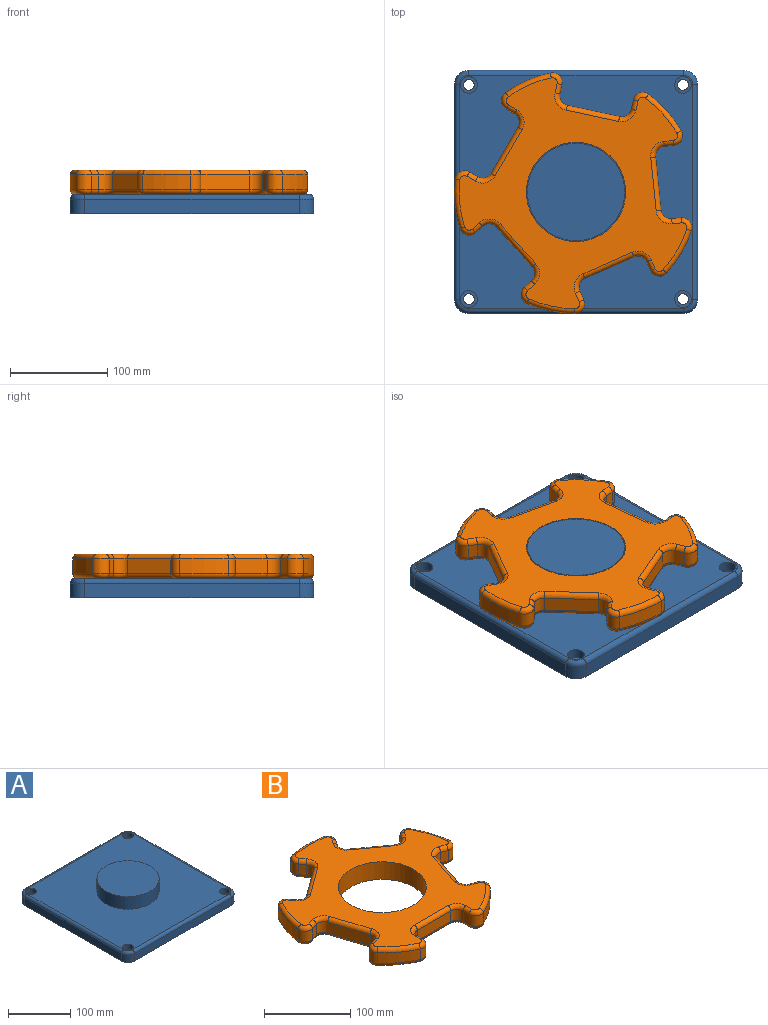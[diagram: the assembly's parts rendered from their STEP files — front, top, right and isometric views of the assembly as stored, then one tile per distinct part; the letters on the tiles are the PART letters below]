
ASSEMBLY  parts=2 mates=1
PART A: 32 faces, bbox 252.5x252.5x45 mm
  f0: plane 220x15mm, normal (1,0,0), area 3300mm2, adj f5,f8,f11,f27
  f1: plane 220x15mm, normal (0,1,0), area 3300mm2, adj f5,f8,f9,f31
  f2: plane 220x15mm, normal (-1,0,0), area 3300mm2, adj f5,f9,f10,f28
  f3: plane 220x15mm, normal (0,-1,0), area 3300mm2, adj f5,f10,f11,f24
  f4: plane 240x240mm, normal (0,0,1), area 48725.4mm2, adj f6,f14,f17,f20,f23,f24,f25,f26
  f5: plane 250x250mm, normal (0,0,-1), area 61926.7mm2, adj f0,f1,f2,f3,f8,f9,f10,f11
  f6: cylinder r=50mm len=100mm, axis (0,0,-1), area 7854mm2, adj f4,f7
  f7: plane 100x100mm, normal (0,0,1), area 7854mm2, adj f6
  f8: cylinder r=15mm len=15mm, axis (0,0,-1), area 353.4mm2, adj f0,f1,f5,f29
  f9: cylinder r=15mm len=15mm, axis (0,0,1), area 353.4mm2, adj f1,f2,f5,f30
  f10: cylinder r=15mm len=15mm, axis (0,0,-1), area 353.4mm2, adj f2,f3,f5,f26
  f11: cylinder r=15mm len=15mm, axis (0,0,1), area 353.4mm2, adj f0,f3,f5,f25
  f12: cylinder r=5.5mm len=11mm, axis (0,0,1), area 345.6mm2, adj f5,f13
  f13: plane 17.25x17.25mm, normal (0,0,1), area 138.7mm2, adj f12,f14
  f14: cylinder r=8.62mm len=17.25mm, axis (0,0,1), area 541.9mm2, adj f4,f13
  f15: cylinder r=5.5mm len=11mm, axis (0,0,1), area 345.6mm2, adj f5,f16
  f16: plane 17.25x17.25mm, normal (0,0,1), area 138.7mm2, adj f15,f17
  f17: cylinder r=8.62mm len=17.25mm, axis (0,0,1), area 541.9mm2, adj f4,f16
  f18: cylinder r=5.5mm len=11mm, axis (0,0,1), area 345.6mm2, adj f5,f19
  f19: plane 17.25x17.25mm, normal (0,0,1), area 138.7mm2, adj f18,f20
  f20: cylinder r=8.62mm len=17.25mm, axis (0,0,1), area 541.9mm2, adj f4,f19
  f21: cylinder r=5.5mm len=11mm, axis (0,0,1), area 345.6mm2, adj f5,f22
  f22: plane 17.25x17.25mm, normal (0,0,1), area 138.7mm2, adj f21,f23
  f23: cylinder r=8.62mm len=17.25mm, axis (0,0,1), area 541.9mm2, adj f4,f22
  f24: cylinder r=5mm len=220mm, axis (-1,0,0), area 1727.9mm2, adj f3,f4,f25,f26
  f25: torus R=10mm, axis (0,0,1), area 162.6mm2, adj f4,f11,f24,f27
  f26: torus R=10mm, axis (0,0,1), area 162.6mm2, adj f4,f10,f24,f28
  f27: cylinder r=5mm len=220mm, axis (0,-1,0), area 1727.9mm2, adj f0,f4,f25,f29
  f28: cylinder r=5mm len=220mm, axis (0,1,0), area 1727.9mm2, adj f2,f4,f26,f30
  f29: torus R=10mm, axis (0,0,1), area 162.6mm2, adj f4,f8,f27,f31
  f30: torus R=10mm, axis (0,0,1), area 162.6mm2, adj f4,f9,f28,f31
  f31: cylinder r=5mm len=220mm, axis (1,0,0), area 1727.9mm2, adj f1,f4,f29,f30
PART B: 123 faces, bbox 268.9x258.5x25 mm
  f0: plane 238.57x229.73mm, normal (0,0,1), area 21505.7mm2, adj f6,f43,f44,f45,f46,f47,f48,f49
  f1: plane 238.57x229.73mm, normal (0,0,-1), area 21505.7mm2, adj f6,f83,f84,f85,f86,f87,f88,f89
  f2: cylinder r=125mm len=40.68mm, axis (0,0,-1), area 759.5mm2, adj f13,f42,f51,f91
  f3: cylinder r=125mm len=47.82mm, axis (0,0,-1), area 759.5mm2, adj f35,f41,f67,f107
  f4: cylinder r=125mm len=50.29mm, axis (0,0,-1), area 759.5mm2, adj f28,f34,f82,f122
  f5: cylinder r=125mm len=47.82mm, axis (0,0,-1), area 759.5mm2, adj f21,f27,f66,f106
  f6: cylinder r=51mm len=102mm, axis (0,0,-1), area 8011.1mm2, adj f0,f1
  f7: cylinder r=125mm len=40.68mm, axis (0,0,-1), area 759.5mm2, adj f14,f20,f50,f90
  f8: plane 15x9.73mm, normal (-1,0,0), area 146mm2, adj f11,f14,f46,f86
  f9: plane 55x15mm, normal (0,-1,0), area 825mm2, adj f11,f12,f43,f83
  f10: plane 15x9.73mm, normal (1,0,0), area 146mm2, adj f12,f13,f47,f87
  f11: cylinder r=10mm len=15mm, axis (0,0,-1), area 235.6mm2, adj f8,f9,f44,f84
  f12: cylinder r=10mm len=15mm, axis (0,0,-1), area 235.6mm2, adj f9,f10,f45,f85
  f13: cylinder r=10mm len=15mm, axis (0,0,-1), area 299.5mm2, adj f2,f10,f49,f89
  f14: cylinder r=10mm len=15mm, axis (0,0,-1), area 299.5mm2, adj f7,f8,f48,f88
  f15: plane 15x9.26mm, normal (-0.31,-0.95,0), area 146mm2, adj f18,f21,f62,f102
  f16: plane 52.31x17mm, normal (0.95,-0.31,0), area 825mm2, adj f18,f19,f58,f98
  f17: plane 15x9.26mm, normal (0.31,0.95,0), area 146mm2, adj f19,f20,f54,f94
  f18: cylinder r=10mm len=15mm, axis (0,0,-1), area 235.6mm2, adj f15,f16,f60,f100
  f19: cylinder r=10mm len=15mm, axis (0,0,-1), area 235.6mm2, adj f16,f17,f56,f96
  f20: cylinder r=10mm len=16.25mm, axis (0,0,-1), area 299.5mm2, adj f7,f17,f52,f92
  f21: cylinder r=10mm len=15mm, axis (0,0,-1), area 299.5mm2, adj f5,f15,f64,f104
  f22: plane 15x7.87mm, normal (0.81,-0.59,0), area 146mm2, adj f25,f28,f78,f118
  f23: plane 44.5x32.33mm, normal (0.59,0.81,0), area 825mm2, adj f25,f26,f74,f114
  f24: plane 15x7.87mm, normal (-0.81,0.59,0), area 146mm2, adj f26,f27,f70,f110
  f25: cylinder r=10mm len=15mm, axis (0,0,-1), area 235.6mm2, adj f22,f23,f76,f116
  f26: cylinder r=10mm len=15mm, axis (0,0,-1), area 235.6mm2, adj f23,f24,f72,f112
  f27: cylinder r=10mm len=16.78mm, axis (0,0,-1), area 299.5mm2, adj f5,f24,f68,f108
  f28: cylinder r=10mm len=15.67mm, axis (0,0,-1), area 299.5mm2, adj f4,f22,f80,f120
  f29: plane 15x7.87mm, normal (0.81,0.59,0), area 146mm2, adj f32,f35,f71,f111
  f30: plane 44.5x32.33mm, normal (-0.59,0.81,0), area 825mm2, adj f32,f33,f75,f115
  f31: plane 15x7.87mm, normal (-0.81,-0.59,0), area 146mm2, adj f33,f34,f79,f119
  f32: cylinder r=10mm len=15mm, axis (0,0,-1), area 235.6mm2, adj f29,f30,f73,f113
  f33: cylinder r=10mm len=15mm, axis (0,0,-1), area 235.6mm2, adj f30,f31,f77,f117
  f34: cylinder r=10mm len=15.67mm, axis (0,0,-1), area 299.5mm2, adj f4,f31,f81,f121
  f35: cylinder r=10mm len=16.78mm, axis (0,0,-1), area 299.5mm2, adj f3,f29,f69,f109
  f36: plane 15x9.26mm, normal (-0.31,0.95,0), area 146mm2, adj f39,f42,f55,f95
  f37: plane 52.31x17mm, normal (-0.95,-0.31,0), area 825mm2, adj f39,f40,f59,f99
  f38: plane 15x9.26mm, normal (0.31,-0.95,0), area 146mm2, adj f40,f41,f63,f103
  f39: cylinder r=10mm len=15mm, axis (0,0,-1), area 235.6mm2, adj f36,f37,f57,f97
  f40: cylinder r=10mm len=15mm, axis (0,0,-1), area 235.6mm2, adj f37,f38,f61,f101
  f41: cylinder r=10mm len=15mm, axis (0,0,-1), area 299.5mm2, adj f3,f38,f65,f105
  f42: cylinder r=10mm len=16.25mm, axis (0,0,-1), area 299.5mm2, adj f2,f36,f53,f93
  f43: cylinder r=5mm len=55mm, axis (1,0,0), area 432mm2, adj f0,f9,f44,f45
  f44: torus R=15mm, axis (0,0,1), area 145.8mm2, adj f0,f11,f43,f46
  f45: torus R=15mm, axis (0,0,1), area 145.8mm2, adj f0,f12,f43,f47
  f46: cylinder r=5mm len=9.73mm, axis (0,-1,0), area 76.4mm2, adj f0,f8,f44,f48
  f47: cylinder r=5mm len=9.73mm, axis (0,1,0), area 76.4mm2, adj f0,f10,f45,f49
  f48: torus R=5mm, axis (0,0,1), area 128.3mm2, adj f0,f14,f46,f50
  f49: torus R=5mm, axis (0,0,1), area 128.3mm2, adj f0,f13,f47,f51
  f50: torus R=120mm, axis (0,0,1), area 391.9mm2, adj f0,f7,f48,f52
  f51: torus R=120mm, axis (0,0,1), area 391.9mm2, adj f0,f2,f49,f53
  f52: torus R=5mm, axis (0,0,1), area 128.3mm2, adj f0,f20,f50,f54
  f53: torus R=5mm, axis (0,0,1), area 128.3mm2, adj f0,f42,f51,f55
  f54: cylinder r=5mm len=10.8mm, axis (-0.95,0.31,0), area 76.4mm2, adj f0,f17,f52,f56
  f55: cylinder r=5mm len=10.8mm, axis (-0.95,-0.31,0), area 76.4mm2, adj f0,f36,f53,f57
  f56: torus R=15mm, axis (0,0,1), area 145.8mm2, adj f0,f19,f54,f58
  f57: torus R=15mm, axis (0,0,1), area 145.8mm2, adj f0,f39,f55,f59
  f58: cylinder r=5mm len=53.85mm, axis (0.31,0.95,0), area 432mm2, adj f0,f16,f56,f60
  f59: cylinder r=5mm len=53.85mm, axis (0.31,-0.95,0), area 432mm2, adj f0,f37,f57,f61
  f60: torus R=15mm, axis (0,0,1), area 145.8mm2, adj f0,f18,f58,f62
  f61: torus R=15mm, axis (0,0,1), area 145.8mm2, adj f0,f40,f59,f63
  f62: cylinder r=5mm len=10.8mm, axis (0.95,-0.31,0), area 76.4mm2, adj f0,f15,f60,f64
  f63: cylinder r=5mm len=10.8mm, axis (0.95,0.31,0), area 76.4mm2, adj f0,f38,f61,f65
  f64: torus R=5mm, axis (0,0,1), area 128.3mm2, adj f0,f21,f62,f66
  f65: torus R=5mm, axis (0,0,1), area 128.3mm2, adj f0,f41,f63,f67
  f66: torus R=120mm, axis (0,0,1), area 391.9mm2, adj f0,f5,f64,f68
  f67: torus R=120mm, axis (0,0,1), area 391.9mm2, adj f0,f3,f65,f69
  f68: torus R=5mm, axis (0,0,1), area 128.3mm2, adj f0,f27,f66,f70
  f69: torus R=5mm, axis (0,0,1), area 128.3mm2, adj f0,f35,f67,f71
  f70: cylinder r=5mm len=10.81mm, axis (-0.59,-0.81,0), area 76.4mm2, adj f0,f24,f68,f72
  f71: cylinder r=5mm len=10.81mm, axis (-0.59,0.81,0), area 76.4mm2, adj f0,f29,f69,f73
  f72: torus R=15mm, axis (0,0,1), area 145.8mm2, adj f0,f26,f70,f74
  f73: torus R=15mm, axis (0,0,1), area 145.8mm2, adj f0,f32,f71,f75
  f74: cylinder r=5mm len=47.44mm, axis (-0.81,0.59,0), area 432mm2, adj f0,f23,f72,f76
  f75: cylinder r=5mm len=47.44mm, axis (-0.81,-0.59,0), area 432mm2, adj f0,f30,f73,f77
  f76: torus R=15mm, axis (0,0,1), area 145.8mm2, adj f0,f25,f74,f78
  f77: torus R=15mm, axis (0,0,1), area 145.8mm2, adj f0,f33,f75,f79
  f78: cylinder r=5mm len=10.81mm, axis (0.59,0.81,0), area 76.4mm2, adj f0,f22,f76,f80
  f79: cylinder r=5mm len=10.81mm, axis (0.59,-0.81,0), area 76.4mm2, adj f0,f31,f77,f81
  f80: torus R=5mm, axis (0,0,1), area 128.3mm2, adj f0,f28,f78,f82
  f81: torus R=5mm, axis (0,0,1), area 128.3mm2, adj f0,f34,f79,f82
  f82: torus R=120mm, axis (0,0,1), area 391.9mm2, adj f0,f4,f80,f81
  f83: cylinder r=5mm len=55mm, axis (-1,0,0), area 432mm2, adj f1,f9,f84,f85
  f84: torus R=15mm, axis (0,0,1), area 145.8mm2, adj f1,f11,f83,f86
  f85: torus R=15mm, axis (0,0,1), area 145.8mm2, adj f1,f12,f83,f87
  f86: cylinder r=5mm len=9.73mm, axis (0,1,0), area 76.4mm2, adj f1,f8,f84,f88
  f87: cylinder r=5mm len=9.73mm, axis (0,-1,0), area 76.4mm2, adj f1,f10,f85,f89
  f88: torus R=5mm, axis (0,0,1), area 128.3mm2, adj f1,f14,f86,f90
  f89: torus R=5mm, axis (0,0,1), area 128.3mm2, adj f1,f13,f87,f91
  f90: torus R=120mm, axis (0,0,1), area 391.9mm2, adj f1,f7,f88,f92
  f91: torus R=120mm, axis (0,0,1), area 391.9mm2, adj f1,f2,f89,f93
  f92: torus R=5mm, axis (0,0,1), area 128.3mm2, adj f1,f20,f90,f94
  f93: torus R=5mm, axis (0,0,1), area 128.3mm2, adj f1,f42,f91,f95
  f94: cylinder r=5mm len=10.8mm, axis (0.95,-0.31,0), area 76.4mm2, adj f1,f17,f92,f96
  f95: cylinder r=5mm len=10.8mm, axis (0.95,0.31,0), area 76.4mm2, adj f1,f36,f93,f97
  f96: torus R=15mm, axis (0,0,1), area 145.8mm2, adj f1,f19,f94,f98
  f97: torus R=15mm, axis (0,0,1), area 145.8mm2, adj f1,f39,f95,f99
  f98: cylinder r=5mm len=53.85mm, axis (-0.31,-0.95,0), area 432mm2, adj f1,f16,f96,f100
  f99: cylinder r=5mm len=53.85mm, axis (-0.31,0.95,0), area 432mm2, adj f1,f37,f97,f101
  f100: torus R=15mm, axis (0,0,1), area 145.8mm2, adj f1,f18,f98,f102
  f101: torus R=15mm, axis (0,0,1), area 145.8mm2, adj f1,f40,f99,f103
  f102: cylinder r=5mm len=10.8mm, axis (-0.95,0.31,0), area 76.4mm2, adj f1,f15,f100,f104
  f103: cylinder r=5mm len=10.8mm, axis (-0.95,-0.31,0), area 76.4mm2, adj f1,f38,f101,f105
  f104: torus R=5mm, axis (0,0,1), area 128.3mm2, adj f1,f21,f102,f106
  f105: torus R=5mm, axis (0,0,1), area 128.3mm2, adj f1,f41,f103,f107
  f106: torus R=120mm, axis (0,0,1), area 391.9mm2, adj f1,f5,f104,f108
  f107: torus R=120mm, axis (0,0,1), area 391.9mm2, adj f1,f3,f105,f109
  f108: torus R=5mm, axis (0,0,1), area 128.3mm2, adj f1,f27,f106,f110
  f109: torus R=5mm, axis (0,0,1), area 128.3mm2, adj f1,f35,f107,f111
  f110: cylinder r=5mm len=10.81mm, axis (0.59,0.81,0), area 76.4mm2, adj f1,f24,f108,f112
  f111: cylinder r=5mm len=10.81mm, axis (0.59,-0.81,0), area 76.4mm2, adj f1,f29,f109,f113
  f112: torus R=15mm, axis (0,0,1), area 145.8mm2, adj f1,f26,f110,f114
  f113: torus R=15mm, axis (0,0,1), area 145.8mm2, adj f1,f32,f111,f115
  f114: cylinder r=5mm len=47.44mm, axis (0.81,-0.59,0), area 432mm2, adj f1,f23,f112,f116
  f115: cylinder r=5mm len=47.44mm, axis (0.81,0.59,0), area 432mm2, adj f1,f30,f113,f117
  f116: torus R=15mm, axis (0,0,1), area 145.8mm2, adj f1,f25,f114,f118
  f117: torus R=15mm, axis (0,0,1), area 145.8mm2, adj f1,f33,f115,f119
  f118: cylinder r=5mm len=10.81mm, axis (-0.59,-0.81,0), area 76.4mm2, adj f1,f22,f116,f120
  f119: cylinder r=5mm len=10.81mm, axis (-0.59,0.81,0), area 76.4mm2, adj f1,f31,f117,f121
  f120: torus R=5mm, axis (0,0,1), area 128.3mm2, adj f1,f28,f118,f122
  f121: torus R=5mm, axis (0,0,1), area 128.3mm2, adj f1,f34,f119,f122
  f122: torus R=120mm, axis (0,0,1), area 391.9mm2, adj f1,f4,f120,f121
PLACE A at identity fixed
PLACE B rot(axis=(0,0,1),95.8deg) t=(0,0,0)mm
MATE revolute A.f6 <-> B.f2  axis (0,0,1) through (0,0,45)mm
